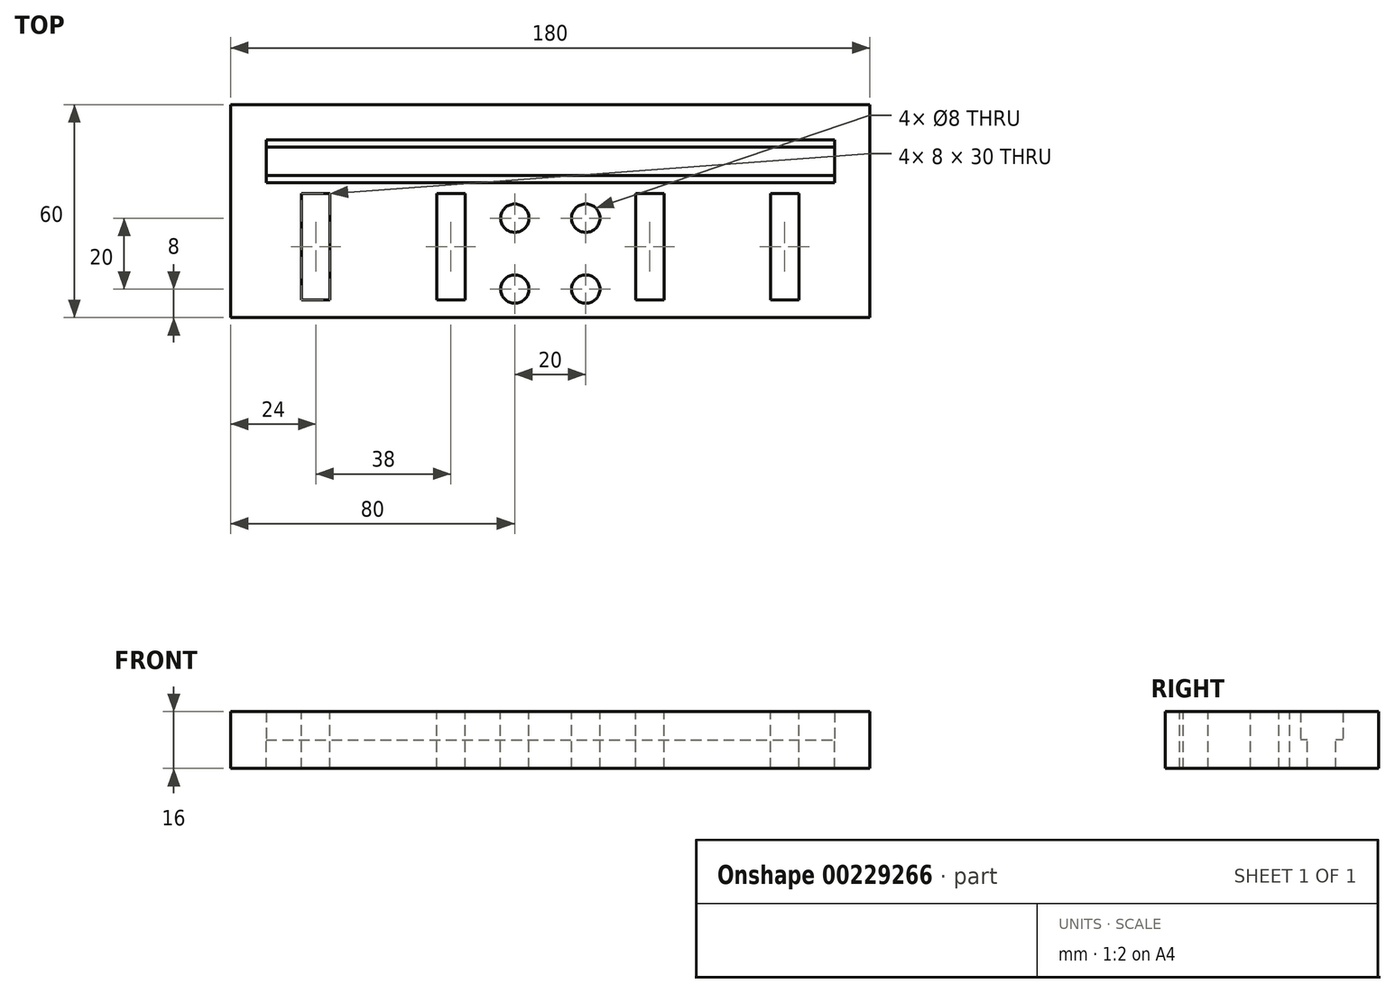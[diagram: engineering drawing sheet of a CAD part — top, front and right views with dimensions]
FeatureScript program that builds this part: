
annotation { "Feature Type Name" : "Feature", "Feature Type Description" : "" }
export const myFeature = defineFeature(function(context is Context, id is Id, definition is map)
    precondition{}
    {
        {
            var Q0;
            Q0=qCreatedBy(makeId("Top.planeOp"),FACE);
            var sketch = newSketch(context, id + "F0", { "sketchPlane" : qUnion([Q0])});
            skLineSegment(sketch, "E0.bottom", {"start": v(-90, 30) * mm, "end": v(90, 30) * mm});
            skLineSegment(sketch, "E0.top", {"start": v(-90, -30) * mm, "end": v(90, -30) * mm});
            skLineSegment(sketch, "E0.left", {"start": v(-90, 30) * mm, "end": v(-90, -30) * mm});
            skLineSegment(sketch, "E0.right", {"start": v(90, 30) * mm, "end": v(90, -30) * mm});
            skPoint(sketch, "E0.middle", {"position": v(0, 0) * mm});
            skCircle(sketch, "E1", {"center": v(-10, -22) * mm, "radius": 4 * mm});
            skCircle(sketch, "E2.0.1.0", {"center": v(-10, -2) * mm, "radius": 4 * mm});
            skCircle(sketch, "E2.1.0.0", {"center": v(10, -22) * mm, "radius": 4 * mm});
            skCircle(sketch, "E2.1.1.0", {"center": v(10, -2) * mm, "radius": 4 * mm});
            skLineSegment(sketch, "E2.direction1", {"start": v(-10, -22) * mm, "end": v(10, -22) * mm, "construction": true});
            skLineSegment(sketch, "E2.direction2", {"start": v(-10, -22) * mm, "end": v(-10, -2) * mm, "construction": true});
            skLineSegment(sketch, "E3.bottom", {"start": v(-80, 20) * mm, "end": v(80, 20) * mm});
            skLineSegment(sketch, "E3.top", {"start": v(-80, 8) * mm, "end": v(80, 8) * mm});
            skLineSegment(sketch, "E3.left", {"start": v(-80, 20) * mm, "end": v(-80, 8) * mm});
            skLineSegment(sketch, "E3.right", {"start": v(80, 20) * mm, "end": v(80, 8) * mm});
            skLineSegment(sketch, "E4.0", {"start": v(-80, 18) * mm, "end": v(80, 18) * mm});
            skLineSegment(sketch, "E4.2", {"start": v(-80, 10) * mm, "end": v(80, 10) * mm});
            skLineSegment(sketch, "E5.bottom", {"start": v(-70, 5) * mm, "end": v(-62, 5) * mm});
            skLineSegment(sketch, "E5.top", {"start": v(-70, -25) * mm, "end": v(-62, -25) * mm});
            skLineSegment(sketch, "E5.left", {"start": v(-70, 5) * mm, "end": v(-70, -25) * mm});
            skLineSegment(sketch, "E5.right", {"start": v(-62, 5) * mm, "end": v(-62, -25) * mm});
            skLineSegment(sketch, "E6.bottom", {"start": v(-32, 5) * mm, "end": v(-24, 5) * mm});
            skLineSegment(sketch, "E6.top", {"start": v(-32, -25) * mm, "end": v(-24, -25) * mm});
            skLineSegment(sketch, "E6.left", {"start": v(-32, 5) * mm, "end": v(-32, -25) * mm});
            skLineSegment(sketch, "E6.right", {"start": v(-24, 5) * mm, "end": v(-24, -25) * mm});
            skLineSegment(sketch, "E7.MirrorCS", {"start": v(70, 5) * mm, "end": v(62, 5) * mm});
            skLineSegment(sketch, "E8.MirrorCS", {"start": v(70, 5) * mm, "end": v(70, -25) * mm});
            skLineSegment(sketch, "E9.MirrorCS", {"start": v(62, 5) * mm, "end": v(62, -25) * mm});
            skLineSegment(sketch, "E10.MirrorCS", {"start": v(70, -25) * mm, "end": v(62, -25) * mm});
            skLineSegment(sketch, "E11.MirrorCS", {"start": v(32, 5) * mm, "end": v(24, 5) * mm});
            skLineSegment(sketch, "E12.MirrorCS", {"start": v(32, 5) * mm, "end": v(32, -25) * mm});
            skLineSegment(sketch, "E13.MirrorCS", {"start": v(32, -25) * mm, "end": v(24, -25) * mm});
            skLineSegment(sketch, "E14.MirrorCS", {"start": v(24, 5) * mm, "end": v(24, -25) * mm});
            skSolve(sketch);
        }
        {
            var Q0;
            Q0 = qSketchRegion(id + "F0", true);
            var Q1;
            Q1=makeQuery(id+"F0.imprint","IMPRINT",FACE,{"disambiguationData":[TD([[makeQuery(id+"F0.imprint","IMPRINT",EDGE,{"derivedFrom":sQuery(id+"F0.wireOp",EDGE,"E3.bottom")}),-1.0]])]});
            var Q2;
            {var subQ0=sQuery(id+"F0.wireOp",EDGE,"E3.top");Q2=makeQuery(id+"F0.imprint","IMPRINT",FACE,{"disambiguationData":[TD([[makeQuery(id+"F0.imprint","IMPRINT",EDGE,{"derivedFrom":subQ0}),1.0]])]});}
            extrude(context, id + "F1", {"entities" : qUnion([Q0, Q1, Q2]), "oppositeDirection" : true, "depth" : 8 * mm});
        }
        {
            var Q0;
            Q0 = qSketchRegion(id + "F0", true);
            extrude(context, id + "F2", {"entities" : qUnion([Q0]), "operationType" : NewBodyOperationType.ADD, "depth" : 8 * mm});
        }
    });
